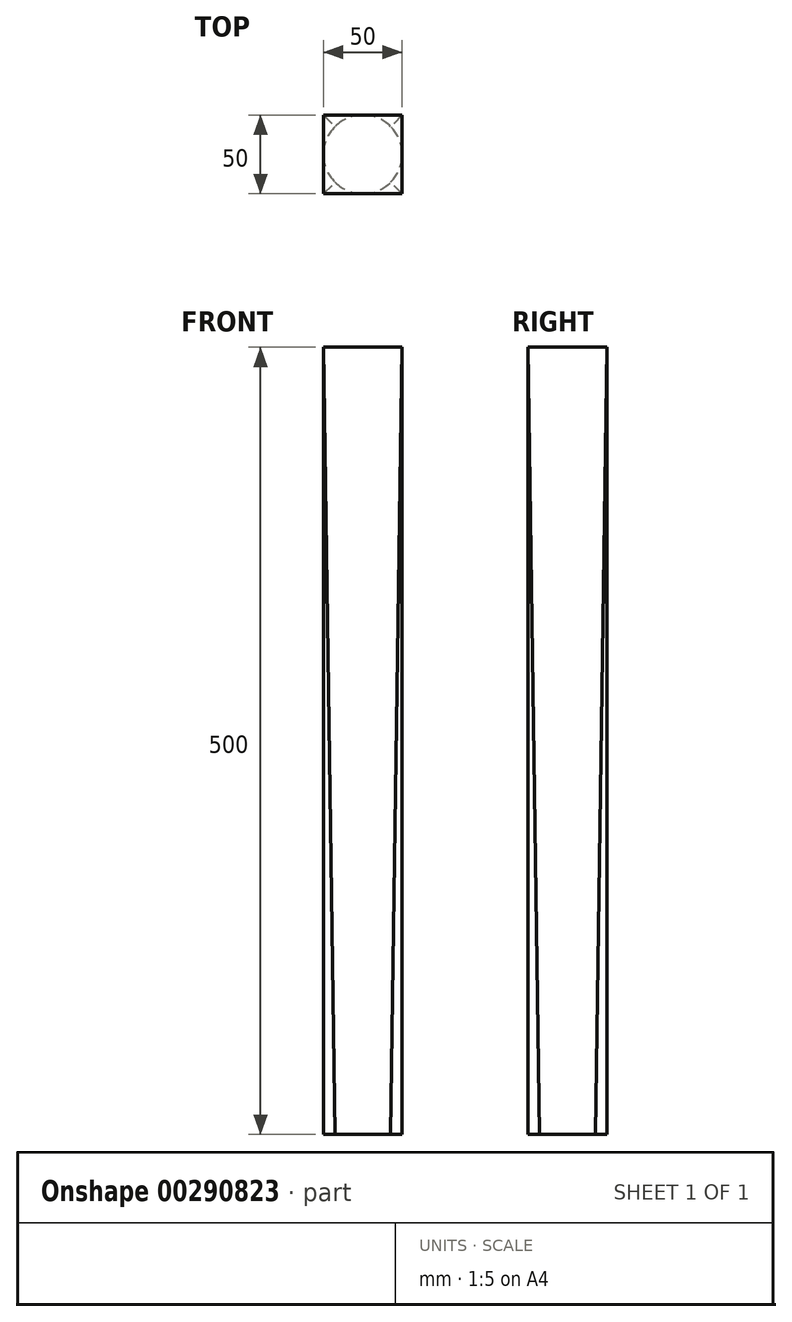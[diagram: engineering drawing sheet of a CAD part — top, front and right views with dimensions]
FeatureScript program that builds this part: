
annotation { "Feature Type Name" : "Feature", "Feature Type Description" : "" }
export const myFeature = defineFeature(function(context is Context, id is Id, definition is map)
    precondition{}
    {
        {
            var Q0;
            Q0=qCreatedBy(makeId("Top.planeOp"),FACE);
            var sketch = newSketch(context, id + "F0", { "sketchPlane" : qUnion([Q0])});
            skCircle(sketch, "E0", {"center": v(0, 0) * mm, "radius": 25 * mm});
            skSolve(sketch);
        }
        {
            var Q0;
            Q0=qCreatedBy(makeId("Top.planeOp"),FACE);
            cPlane(context, id + "F1", {"entities" : qUnion([Q0]), "cplaneType" : CPlaneType.OFFSET, "offset" : 500 * mm, "width" : 150 * mm, "height" : 150 * mm});
        }
        {
            var Q0;
            Q0=qCreatedBy(id+"F1.planeOp",FACE);
            var sketch = newSketch(context, id + "F2", { "sketchPlane" : qUnion([Q0])});
            skLineSegment(sketch, "E1.bottom", {"start": v(25, 25) * mm, "end": v(-25, 25) * mm});
            skLineSegment(sketch, "E1.top", {"start": v(25, -25) * mm, "end": v(-25, -25) * mm});
            skLineSegment(sketch, "E1.left", {"start": v(25, 25) * mm, "end": v(25, -25) * mm});
            skLineSegment(sketch, "E1.right", {"start": v(-25, 25) * mm, "end": v(-25, -25) * mm});
            skPoint(sketch, "E1.middle", {"position": v(0, 0) * mm});
            skSolve(sketch);
        }
        {
            var Q0;
            Q0=makeQuery(id+"F2.imprint","IMPRINT",FACE,{"disambiguationData":[TD([[makeQuery(id+"F2.imprint","IMPRINT",EDGE,{"derivedFrom":sQuery(id+"F2.wireOp",EDGE,"E1.bottom")}),1.0]])]});
            var Q1;
            Q1=makeQuery(id+"F0.imprint","IMPRINT",FACE,{"disambiguationData":[TD([[makeQuery(id+"F0.imprint","IMPRINT",EDGE,{"derivedFrom":sQuery(id+"F0.wireOp",EDGE,"E0")}),1.0]])]});
            loft(context, id + "F3", {"sheetProfilesArray" : [{ "sheetProfileEntities" : qUnion([Q0]) }, { "sheetProfileEntities" : qUnion([Q1]) }]});
        }
    });
